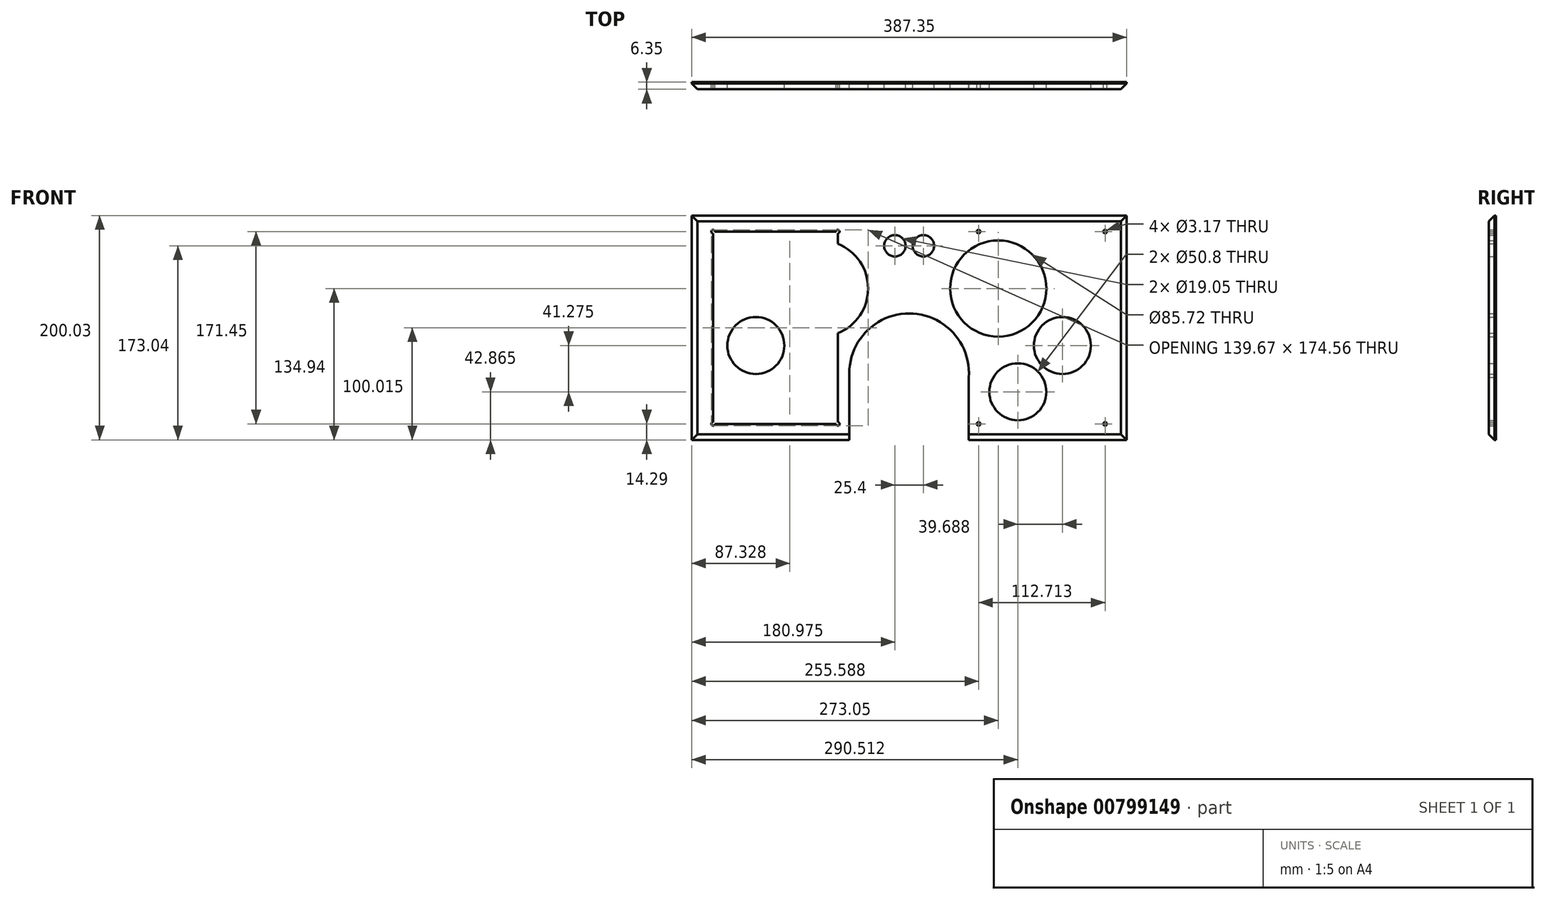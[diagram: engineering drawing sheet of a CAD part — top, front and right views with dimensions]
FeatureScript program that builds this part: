
annotation { "Feature Type Name" : "Feature", "Feature Type Description" : "" }
export const myFeature = defineFeature(function(context is Context, id is Id, definition is map)
    precondition{}
    {
        {
            var Q0;
            Q0=qCreatedBy(makeId("Front.planeOp"),FACE);
            var sketch = newSketch(context, id + "F0", { "sketchPlane" : qUnion([Q0])});
            skLineSegment(sketch, "E0", {"start": v(0, 0) * mm, "end": v(349.25, 0) * mm});
            skLineSegment(sketch, "E1", {"start": v(349.25, 0) * mm, "end": v(349.25, -171.45) * mm});
            skCircle(sketch, "E2", {"center": v(0, 0) * mm, "radius": 1.59 * mm});
            skCircle(sketch, "E3", {"center": v(349.25, 0) * mm, "radius": 1.59 * mm});
            skCircle(sketch, "E4", {"center": v(349.25, -171.45) * mm, "radius": 1.59 * mm});
            skLineSegment(sketch, "E5", {"start": v(174.63, 0) * mm, "end": v(174.63, -129.92) * mm});
            skLineSegment(sketch, "E6", {"start": v(0, 0) * mm, "end": v(0, -171.45) * mm});
            skCircle(sketch, "E7", {"center": v(0, -171.45) * mm, "radius": 1.59 * mm});
            skLineSegment(sketch, "E8", {"start": v(111.13, 0) * mm, "end": v(111.13, 25.68) * mm});
            skCircle(sketch, "E9", {"center": v(111.13, 0) * mm, "radius": 1.59 * mm});
            skLineSegment(sketch, "E10", {"start": v(236.54, 0) * mm, "end": v(236.54, 24.94) * mm});
            skCircle(sketch, "E11", {"center": v(236.54, 0) * mm, "radius": 1.59 * mm});
            skLineSegment(sketch, "E12", {"start": v(0, -171.45) * mm, "end": v(111.13, -171.45) * mm});
            skCircle(sketch, "E13", {"center": v(111.13, -171.45) * mm, "radius": 1.59 * mm});
            skLineSegment(sketch, "E14", {"start": v(236.54, 0) * mm, "end": v(236.54, -171.45) * mm});
            skLineSegment(sketch, "E15", {"start": v(236.54, -171.45) * mm, "end": v(349.25, -171.45) * mm});
            skCircle(sketch, "E16", {"center": v(236.54, -171.45) * mm, "radius": 1.59 * mm});
            skLineSegment(sketch, "E17", {"start": v(111.13, -171.45) * mm, "end": v(111.13, 0) * mm});
            skLineSegment(sketch, "E18", {"start": v(174.63, -73.02) * mm, "end": v(212.58, -73.02) * mm});
            skLineSegment(sketch, "E19", {"start": v(121.44, -129.92) * mm, "end": v(227.8, -129.92) * mm});
            skLineSegment(sketch, "E20", {"start": v(121.44, -129.92) * mm, "end": v(121.44, -196.93) * mm});
            skLineSegment(sketch, "E21", {"start": v(227.8, -129.92) * mm, "end": v(227.8, -201.06) * mm});
            skCircle(sketch, "E22", {"center": v(174.63, -126.33) * mm, "radius": 53.3 * mm});
            skCircle(sketch, "E23", {"center": v(271.46, -142.88) * mm, "radius": 25.4 * mm});
            skCircle(sketch, "E24", {"center": v(311.15, -101.6) * mm, "radius": 25.4 * mm});
            skCircle(sketch, "E25", {"center": v(254, -50.8) * mm, "radius": 42.86 * mm});
            skCircle(sketch, "E26", {"center": v(187.33, -12.7) * mm, "radius": 9.53 * mm});
            skCircle(sketch, "E27", {"center": v(161.93, -12.7) * mm, "radius": 9.53 * mm});
            skCircle(sketch, "E28.MirrorC", {"center": v(95.25, -50.8) * mm, "radius": 42.86 * mm});
            skCircle(sketch, "E29.MirrorC", {"center": v(38.1, -101.6) * mm, "radius": 25.4 * mm});
            skCircle(sketch, "E30.MirrorC", {"center": v(77.79, -142.88) * mm, "radius": 25.4 * mm});
            skLineSegment(sketch, "E31", {"start": v(-19.05, 14.29) * mm, "end": v(-19.05, -185.74) * mm});
            skLineSegment(sketch, "E32", {"start": v(-19.05, -185.74) * mm, "end": v(368.3, -185.74) * mm});
            skLineSegment(sketch, "E33", {"start": v(-19.05, 14.29) * mm, "end": v(368.3, 14.29) * mm});
            skLineSegment(sketch, "E34", {"start": v(368.3, -185.74) * mm, "end": v(368.3, 14.29) * mm});
            skSolve(sketch);
        }
        {
            var Q0;
            Q0=makeQuery(id+"F0.imprint","IMPRINT",FACE,{"disambiguationData":[TD([[makeQuery(id+"F0.imprint","IMPRINT",EDGE,{"derivedFrom":sQuery(id+"F0.wireOp",EDGE,"E29.MirrorC")}),1.0]])]});
            var Q1;
            Q1=makeQuery(id+"F0.imprint","IMPRINT",FACE,{"disambiguationData":[TD([[makeQuery(id+"F0.imprint","IMPRINT",EDGE,{"derivedFrom":sQuery(id+"F0.wireOp",EDGE,"E27")}),-1.0]])]});
            var Q2;
            Q2=makeQuery(id+"F0.imprint","IMPRINT",FACE,{"disambiguationData":[TD([[makeQuery(id+"F0.imprint","IMPRINT",EDGE,{"derivedFrom":sQuery(id+"F0.wireOp",EDGE,"E26")}),-1.0]])]});
            var Q3;
            {var subQ1=sQuery(id+"F0.wireOp",EDGE,"E0");var subQ7=makeQuery(id+"F0.imprint","INTERSECT",VERTEX,{"derivedFrom":[subQ1,sQuery(id+"F0.wireOp",EDGE,"E5")]});Q3=makeQuery(id+"F0.imprint","IMPRINT",FACE,{"disambiguationData":[TD([[makeQuery(id+"F0.imprint","IMPRINT",EDGE,{"disambiguationData":[TD([[subQ7,1.0]])],"derivedFrom":subQ1}),1.0]])]});}
            var Q4;
            Q4=makeQuery(id+"F0.imprint","IMPRINT",FACE,{"disambiguationData":[TD([[makeQuery(id+"F0.imprint","IMPRINT",EDGE,{"derivedFrom":sQuery(id+"F0.wireOp",EDGE,"E23")}),-1.0]])]});
            extrude(context, id + "F1", {"entities" : qUnion([Q0, Q1, Q2, Q3, Q4]), "depth" : 6.35 * mm, "offsetDistance" : 25.4 * mm});
        }
        {
            var Q0;
            Q0=makeQuery(id+"F1.opExtrude","CAP_EDGE",EDGE,{"disambiguationData":[OSD([sQuery(id+"F0.wireOp",EDGE,"E33")])],"isStart":false});
            var Q1;
            {var subQ0=sQuery(id+"F0.wireOp",EDGE,"E32");Q1=makeQuery(id+"F1.opExtrude","CAP_EDGE",EDGE,{"disambiguationData":[OSD([subQ0]),TDD([makeQuery(id+"F0.imprint","IMPRINT",EDGE,{"disambiguationData":[TD([[makeQuery(id+"F0.imprint","INTERSECT",VERTEX,{"derivedFrom":[subQ0,sQuery(id+"F0.wireOp",EDGE,"E34")]}),1.0]])],"derivedFrom":subQ0})])],"isStart":false});}
            var Q2;
            Q2=makeQuery(id+"F1.opExtrude","CAP_EDGE",EDGE,{"disambiguationData":[OSD([sQuery(id+"F0.wireOp",EDGE,"E34")])],"isStart":false});
            var Q3;
            {var subQ0=sQuery(id+"F0.wireOp",EDGE,"E32");Q3=makeQuery(id+"F1.opExtrude","CAP_EDGE",EDGE,{"disambiguationData":[OSD([subQ0]),TDD([makeQuery(id+"F0.imprint","IMPRINT",EDGE,{"disambiguationData":[TD([[makeQuery(id+"F0.imprint","INTERSECT",VERTEX,{"derivedFrom":[sQuery(id+"F0.wireOp",EDGE,"E31"),subQ0]}),-1.0]])],"derivedFrom":subQ0})])],"isStart":false});}
            var Q4;
            Q4=makeQuery(id+"F1.opExtrude","CAP_EDGE",EDGE,{"disambiguationData":[OSD([sQuery(id+"F0.wireOp",EDGE,"E31")])],"isStart":false});
            chamfer(context, id + "F2", {"entities" : qUnion([Q0, Q1, Q2, Q3, Q4]), "width" : 5.08 * mm, "tangentPropagation" : true});
        }
    });
